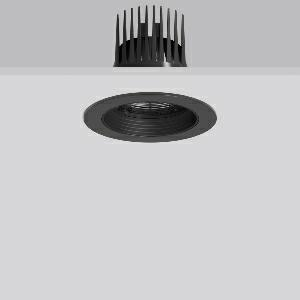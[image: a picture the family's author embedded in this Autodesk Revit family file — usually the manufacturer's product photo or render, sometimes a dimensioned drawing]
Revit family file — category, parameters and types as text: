
# Revit family: heledon_maxi_e_901789_003_2_9d05
name_source: partatom
category: Lighting Fixtures
units: mm (PartAtom-declared; Revit-internal decimal feet)

## family parameters
Cut with Voids When Loaded = No
Host = Face
Light Source = No
Part Type = Normal
Room Calculation Point = No
Round Connector Dimension = Use Diameter
Shared = No

## types (1)
- HELEDON maxi E (1 x LED Modul 927 bakery, 2850 lm, 2700)
    Apparent Load = 33 VA
    Approval mark = CE
    CIE Flux Codes = 96 99 100 100 100
    Color Rendering = 90
    Color Temperature = 2700
    Default Elevation = 1800 mm
    Description = Series: HELEDON maxi
Round recessed downlight. Housing: die-cast aluminium, powder-coated. Black plastic ring and recessed LED to prevent glare from the side. Optical assembly with lens made of plastic (polycarbonate) for the best homogeneous light distribution - can be changed without tools. Special LED for illumination of pastries included. Suitable for Recessed ceiling mounting. Installation without tools thanks to spring fastening system. Including separate LED converter with connecting cable 600 mm.High quality converter without flickering and stroboscopic effect. Through-wiring box (5 pole) available as accessory. The following accessories can be mounted without use of tools: interchangeable lenses, decorative glasses, honeycomb louvre, clear and frosted diffusers, white interchangeable plastic ring. 
Colour: deep black, matt (RAL 9005)
Diameter: 162 mm
Height: 3 mm
Cut-out diameter: 152 mm
Recess height: 200 mm
Luminaire: recess height: 135 mm
Lamp: LED
Socket: without socket
Colour temperature: bakery
Colour rendering index (CRI): 97
System power: 33 W
Rated luminous flux: 2850 lm
Luminous efficiency: 86 lm/W
Control gear: Regulated power supply
Protection class: II
Type of protection: IP 20
    Height = 0 mm  [stored 0 ft]
    Lamp = 1 x LED Modul 927 bakery
    Lamp Light Flux = 2850 lm
    Lamp count = 1
    Length = 162 mm
    Lifetime = 50000 h
    Luminous efficacy = 86 lm/W
    Manufacturer = RZB
    ModVariant = No
    Model = 901789.003.2
    Mounting Place = Ceiling
    Mounting Type = Recessed
    Number of Poles = 1
    OnlyDefault = Yes
    Power Factor = 1
    Product Name = HELEDON maxi E
    Product group = Recessed downlights
    ProductGroupID = 402
    Protection Class = Protection class II
    Protection Degree = IP 20
    RLX_Detail_Level = 1
    RLX_Emergency_Light_Flux = 0 lm
    RLX_Emergency_Type = 0
    RLX_Emergency_Type_DB = No
    RlxData = <blob elided: 121005 chars, md5=59bef01c>
    Socket = socket
    Standby Power = 0 W
    System Light Flux = 2850 lm
    System Power = 33 W
    Type Comments = Product without accessories
    Type Image = 901663.003.jpg
    URL = http://relux.com
    VarID = ---
    Voltage = 230 V
    Voltage Range = 220-240 V
    Weight = 0.00 kg
    Width = 0 mm  [stored 0 ft]

note: [stored X ft] marks values corroborated as IEEE doubles in the binary element streams (Revit-internal decimal feet)

## geometry (parser evidence)
native form markers: Blend x4, Sweep x12
no freeform markers — native parametric forms only
